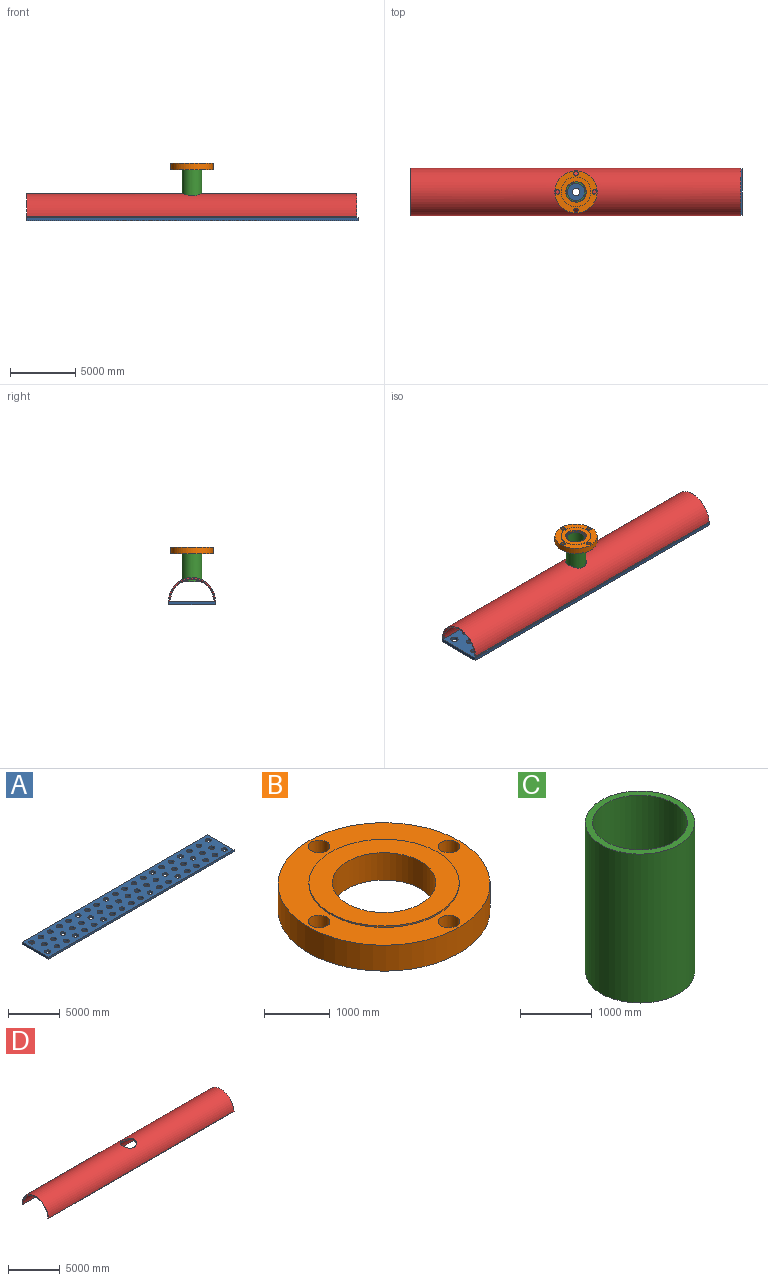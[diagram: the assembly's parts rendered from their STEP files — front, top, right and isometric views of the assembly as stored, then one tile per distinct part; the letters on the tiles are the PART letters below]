
ASSEMBLY  parts=4 mates=3
PART A: 65 faces, bbox 25400x3556x241.3 mm
  f0: cylinder r=279.4mm len=558.8mm, axis (0,0,1), area 423607.5mm2, adj f60,f61
  f1: cylinder r=279.4mm len=558.8mm, axis (0,0,1), area 423607.5mm2, adj f60,f61
  f2: cylinder r=279.4mm len=558.8mm, axis (0,0,1), area 423607.5mm2, adj f60,f61
  f3: cylinder r=279.4mm len=558.8mm, axis (0,0,1), area 423607.5mm2, adj f60,f61
  f4: cylinder r=279.4mm len=558.8mm, axis (0,0,1), area 423607.5mm2, adj f60,f61
  f5: cylinder r=279.4mm len=558.8mm, axis (0,0,1), area 423607.5mm2, adj f60,f61
  f6: cylinder r=279.4mm len=558.8mm, axis (0,0,1), area 423607.5mm2, adj f60,f61
  f7: cylinder r=279.4mm len=558.8mm, axis (0,0,1), area 423607.5mm2, adj f60,f61
  f8: cylinder r=279.4mm len=558.8mm, axis (0,0,1), area 423607.5mm2, adj f60,f61
  f9: cylinder r=279.4mm len=558.8mm, axis (0,0,1), area 423607.5mm2, adj f60,f61
  f10: cylinder r=279.4mm len=558.8mm, axis (0,0,1), area 423607.5mm2, adj f60,f61
  f11: cylinder r=279.4mm len=558.8mm, axis (0,0,1), area 423607.5mm2, adj f60,f61
  f12: cylinder r=279.4mm len=558.8mm, axis (0,0,1), area 423607.5mm2, adj f60,f61
  f13: cylinder r=279.4mm len=558.8mm, axis (0,0,1), area 423607.5mm2, adj f60,f61
  f14: cylinder r=279.4mm len=558.8mm, axis (0,0,1), area 423607.5mm2, adj f60,f61
  f15: cylinder r=279.4mm len=558.8mm, axis (0,0,1), area 423607.5mm2, adj f60,f61
  f16: cylinder r=279.4mm len=558.8mm, axis (0,0,1), area 423607.5mm2, adj f60,f61
  f17: cylinder r=279.4mm len=558.8mm, axis (0,0,1), area 423607.5mm2, adj f60,f61
  f18: cylinder r=279.4mm len=558.8mm, axis (0,0,1), area 423607.5mm2, adj f60,f61
  f19: cylinder r=279.4mm len=558.8mm, axis (0,0,1), area 423607.5mm2, adj f60,f61
  f20: cylinder r=279.4mm len=558.8mm, axis (0,0,1), area 423607.5mm2, adj f60,f61
  f21: cylinder r=279.4mm len=558.8mm, axis (0,0,1), area 423607.5mm2, adj f60,f61
  f22: cylinder r=279.4mm len=558.8mm, axis (0,0,1), area 423607.5mm2, adj f60,f61
  f23: cylinder r=279.4mm len=558.8mm, axis (0,0,1), area 423607.5mm2, adj f60,f61
  f24: cylinder r=279.4mm len=558.8mm, axis (0,0,1), area 423607.5mm2, adj f60,f61
  f25: cylinder r=279.4mm len=558.8mm, axis (0,0,1), area 423607.5mm2, adj f60,f61
  f26: cylinder r=279.4mm len=558.8mm, axis (0,0,1), area 423607.5mm2, adj f60,f61
  f27: cylinder r=279.4mm len=558.8mm, axis (0,0,1), area 423607.5mm2, adj f60,f61
  f28: cylinder r=279.4mm len=558.8mm, axis (0,0,1), area 423607.5mm2, adj f60,f61
  f29: cylinder r=279.4mm len=558.8mm, axis (0,0,1), area 423607.5mm2, adj f60,f61
  f30: cylinder r=279.4mm len=558.8mm, axis (0,0,1), area 423607.5mm2, adj f60,f61
  f31: cylinder r=279.4mm len=558.8mm, axis (0,0,1), area 423607.5mm2, adj f60,f61
  f32: cylinder r=279.4mm len=558.8mm, axis (0,0,1), area 423607.5mm2, adj f60,f61
  f33: cylinder r=279.4mm len=558.8mm, axis (0,0,1), area 423607.5mm2, adj f60,f61
  f34: cylinder r=279.4mm len=558.8mm, axis (0,0,1), area 423607.5mm2, adj f60,f61
  f35: cylinder r=279.4mm len=558.8mm, axis (0,0,1), area 423607.5mm2, adj f60,f61
  f36: cylinder r=279.4mm len=558.8mm, axis (0,0,1), area 423607.5mm2, adj f60,f61
  f37: cylinder r=279.4mm len=558.8mm, axis (0,0,1), area 423607.5mm2, adj f60,f61
  f38: cylinder r=279.4mm len=558.8mm, axis (0,0,1), area 423607.5mm2, adj f60,f61
  f39: cylinder r=279.4mm len=558.8mm, axis (0,0,1), area 423607.5mm2, adj f60,f61
  f40: cylinder r=279.4mm len=558.8mm, axis (0,0,1), area 423607.5mm2, adj f60,f61
  f41: cylinder r=279.4mm len=558.8mm, axis (0,0,1), area 423607.5mm2, adj f60,f61
  f42: cylinder r=279.4mm len=558.8mm, axis (0,0,1), area 423607.5mm2, adj f60,f61
  f43: cylinder r=279.4mm len=558.8mm, axis (0,0,1), area 423607.5mm2, adj f60,f61
  f44: cylinder r=279.4mm len=558.8mm, axis (0,0,1), area 423607.5mm2, adj f60,f61
  f45: cylinder r=279.4mm len=558.8mm, axis (0,0,1), area 423607.5mm2, adj f60,f61
  f46: cylinder r=279.4mm len=558.8mm, axis (0,0,1), area 423607.5mm2, adj f60,f61
  f47: cylinder r=279.4mm len=558.8mm, axis (0,0,1), area 423607.5mm2, adj f60,f61
  f48: cylinder r=279.4mm len=558.8mm, axis (0,0,1), area 423607.5mm2, adj f60,f61
  f49: cylinder r=279.4mm len=558.8mm, axis (0,0,1), area 423607.5mm2, adj f60,f61
  f50: cylinder r=279.4mm len=558.8mm, axis (0,0,1), area 423607.5mm2, adj f60,f61
  f51: cylinder r=279.4mm len=558.8mm, axis (0,0,1), area 423607.5mm2, adj f60,f61
  f52: cylinder r=279.4mm len=558.8mm, axis (0,0,1), area 423607.5mm2, adj f60,f61
  f53: cylinder r=279.4mm len=558.8mm, axis (0,0,1), area 423607.5mm2, adj f60,f61
  f54: cylinder r=279.4mm len=558.8mm, axis (0,0,1), area 423607.5mm2, adj f60,f61
  f55: cylinder r=279.4mm len=558.8mm, axis (0,0,1), area 423607.5mm2, adj f60,f61
  f56: plane 3556x241.3mm, normal (-1,0,0), area 858062.8mm2, adj f57,f59,f60,f61
  f57: plane 25400x241.3mm, normal (0,-1,0), area 6129020mm2, adj f56,f58,f60,f61
  f58: plane 3556x241.3mm, normal (1,0,0), area 858062.8mm2, adj f57,f59,f60,f61
  f59: plane 25400x241.3mm, normal (0,1,0), area 6129020mm2, adj f56,f58,f60,f61
  f60: plane 25400x3556mm, normal (0,0,1), area 75852861.2mm2, adj f0,f1,f2,f3,f4,f5,f6,f7
  f61: plane 25400x3556mm, normal (0,0,-1), area 75852861.2mm2, adj f0,f1,f2,f3,f4,f5,f6,f7
  f62: cylinder r=279.4mm len=558.8mm, axis (0,0,1), area 423607.5mm2, adj f60,f61
  f63: cylinder r=279.4mm len=558.8mm, axis (0,0,1), area 423607.5mm2, adj f60,f61
  f64: cylinder r=279.4mm len=558.8mm, axis (0,0,1), area 423607.5mm2, adj f60,f61
PART B: 10 faces, bbox 3225.8x3225.8x508 mm
  f0: cylinder r=1612.9mm len=3225.8mm, axis (0,0,-1), area 4890740.6mm2, adj f1,f2
  f1: plane 3225.8x3225.8mm, normal (0,0,1), area 3725820.1mm2, adj f0,f4,f6,f7,f8,f9
  f2: plane 3225.8x3225.8mm, normal (0,0,-1), area 5882367.1mm2, adj f0,f3,f6,f7,f8,f9
  f3: cylinder r=787.4mm len=1574.8mm, axis (0,0,-1), area 2513269.1mm2, adj f2,f5
  f4: cylinder r=1143mm len=2286mm, axis (0,0,-1), area 182414.7mm2, adj f1,f5
  f5: plane 2286x2286mm, normal (0,0,1), area 2156547mm2, adj f3,f4
  f6: cylinder r=165.1mm len=482.6mm, axis (0,0,1), area 500627mm2, adj f1,f2
  f7: cylinder r=165.1mm len=482.6mm, axis (0,0,1), area 500627mm2, adj f1,f2
  f8: cylinder r=165.1mm len=482.6mm, axis (0,0,1), area 500627mm2, adj f1,f2
  f9: cylinder r=165.1mm len=482.6mm, axis (0,0,1), area 500627mm2, adj f1,f2
PART C: 4 faces, bbox 1524x1524x2540 mm
  f0: cylinder r=762mm len=2540mm, axis (0,0,-1), area 12160979.5mm2, adj f1,f2
  f1: plane 1524x1524mm, normal (0,0,1), area 454009.9mm2, adj f0,f3
  f2: plane 1524x1524mm, normal (0,0,-1), area 454009.9mm2, adj f0,f3
  f3: cylinder r=660.4mm len=2540mm, axis (0,0,1), area 10539515.6mm2, adj f1,f2
PART D: 11 faces, bbox 25247.6x3603.3x1803.4 mm
  f0: cylinder r=1803.4mm len=25247.6mm, axis (-1,0,0), area 137026077.6mm2, adj f4,f5,f8,f9,f10
  f1: cylinder r=1651mm len=25095.2mm, axis (-1,0,0), area 128154372mm2, adj f2,f3,f6,f7,f10
  f2: plane 25244.24x74.52mm, normal (0,0,-1), area 1875604.6mm2, adj f1,f6,f7,f8
  f3: plane 25244.24x74.52mm, normal (0,0,-1), area 1875604.6mm2, adj f1,f6,f7,f9
  f4: plane 3603.29x1801.64mm, normal (1,0,0), area 416354mm2, adj f0,f6,f8,f9
  f5: plane 3603.29x1801.64mm, normal (-1,0,0), area 416354mm2, adj f0,f7,f8,f9
  f6: cone r=1727.2mm half-angle=45deg, axis (1,0,0), area 571836.7mm2, adj f1,f2,f3,f4,f8,f9
  f7: cone r=1651mm half-angle=45deg, axis (-1,0,0), area 571836.7mm2, adj f1,f2,f3,f5,f8,f9
  f8: plane 25247.6x79.56mm, normal (0,-0.72,-0.69), area 2780123.9mm2, adj f0,f2,f4,f5,f6,f7
  f9: plane 25247.6x79.56mm, normal (0,0.72,-0.69), area 2780123.9mm2, adj f0,f3,f4,f5,f6,f7
  f10: cylinder r=787.4mm len=1574.8mm, axis (0,0,-1), area 798814.3mm2, adj f0,f1
PLACE A t=(-13306.21,-1695.08,-3401.93)mm
PLACE B t=(-606.21,82.92,522.37)mm
PLACE C t=(-606.21,82.92,-1636.63)mm
PLACE D t=(-636.2,82.92,-3111.33)mm
MATE slider C.f3 <-> B.f3  axis (0,0,1) through (-606.21,82.92,903.37)mm
MATE cylindrical D.f10 <-> C.f0  axis (0,0,-1) through (-606.21,82.92,-1484.23)mm
MATE cylindrical A.f9 <-> C.f0  axis (0,0,1) through (-606.21,82.92,-3160.63)mm
